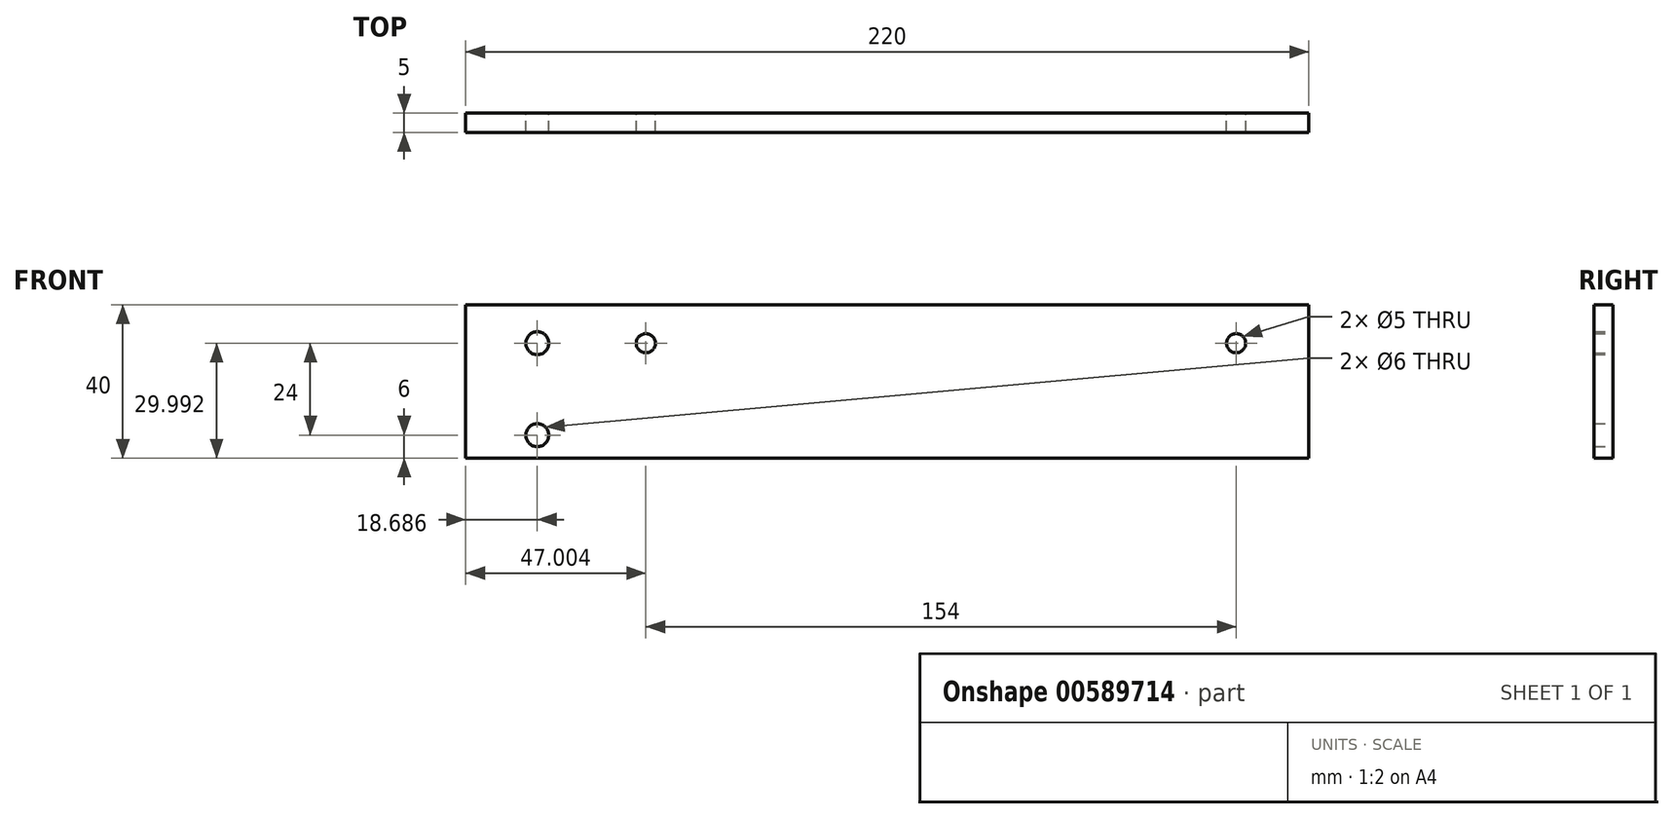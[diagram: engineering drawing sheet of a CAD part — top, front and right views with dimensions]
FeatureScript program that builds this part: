
annotation { "Feature Type Name" : "Feature", "Feature Type Description" : "" }
export const myFeature = defineFeature(function(context is Context, id is Id, definition is map)
    precondition{}
    {
        {
            var Q0;
            Q0=qCreatedBy(makeId("Front.planeOp"),FACE);
            var sketch = newSketch(context, id + "F0", { "sketchPlane" : qUnion([Q0])});
            skLineSegment(sketch, "E0.bottom", {"start": v(110, 20) * mm, "end": v(-110, 20) * mm});
            skLineSegment(sketch, "E0.top", {"start": v(110, -20) * mm, "end": v(-110, -20) * mm});
            skLineSegment(sketch, "E0.left", {"start": v(110, 20) * mm, "end": v(110, -20) * mm});
            skLineSegment(sketch, "E0.right", {"start": v(-110, 20) * mm, "end": v(-110, -20) * mm});
            skPoint(sketch, "E0.middle", {"position": v(0, 0) * mm});
            skCircle(sketch, "E1", {"center": v(-91.31, 10) * mm, "radius": 3 * mm});
            skCircle(sketch, "E2", {"center": v(-91.31, -14) * mm, "radius": 3 * mm});
            skCircle(sketch, "E3", {"center": v(-63, 10) * mm, "radius": 2.5 * mm});
            skCircle(sketch, "E4", {"center": v(91, 10) * mm, "radius": 2.5 * mm});
            skSolve(sketch);
        }
        {
            var Q0;
            Q0=makeQuery(id+"F0.imprint","IMPRINT",FACE,{"disambiguationData":[TD([[makeQuery(id+"F0.imprint","IMPRINT",EDGE,{"derivedFrom":sQuery(id+"F0.wireOp",EDGE,"E0.bottom")}),1.0]])]});
            extrude(context, id + "F1", {"entities" : qUnion([Q0]), "depth" : 5 * mm, "offsetDistance" : 25.4 * mm});
        }
    });
